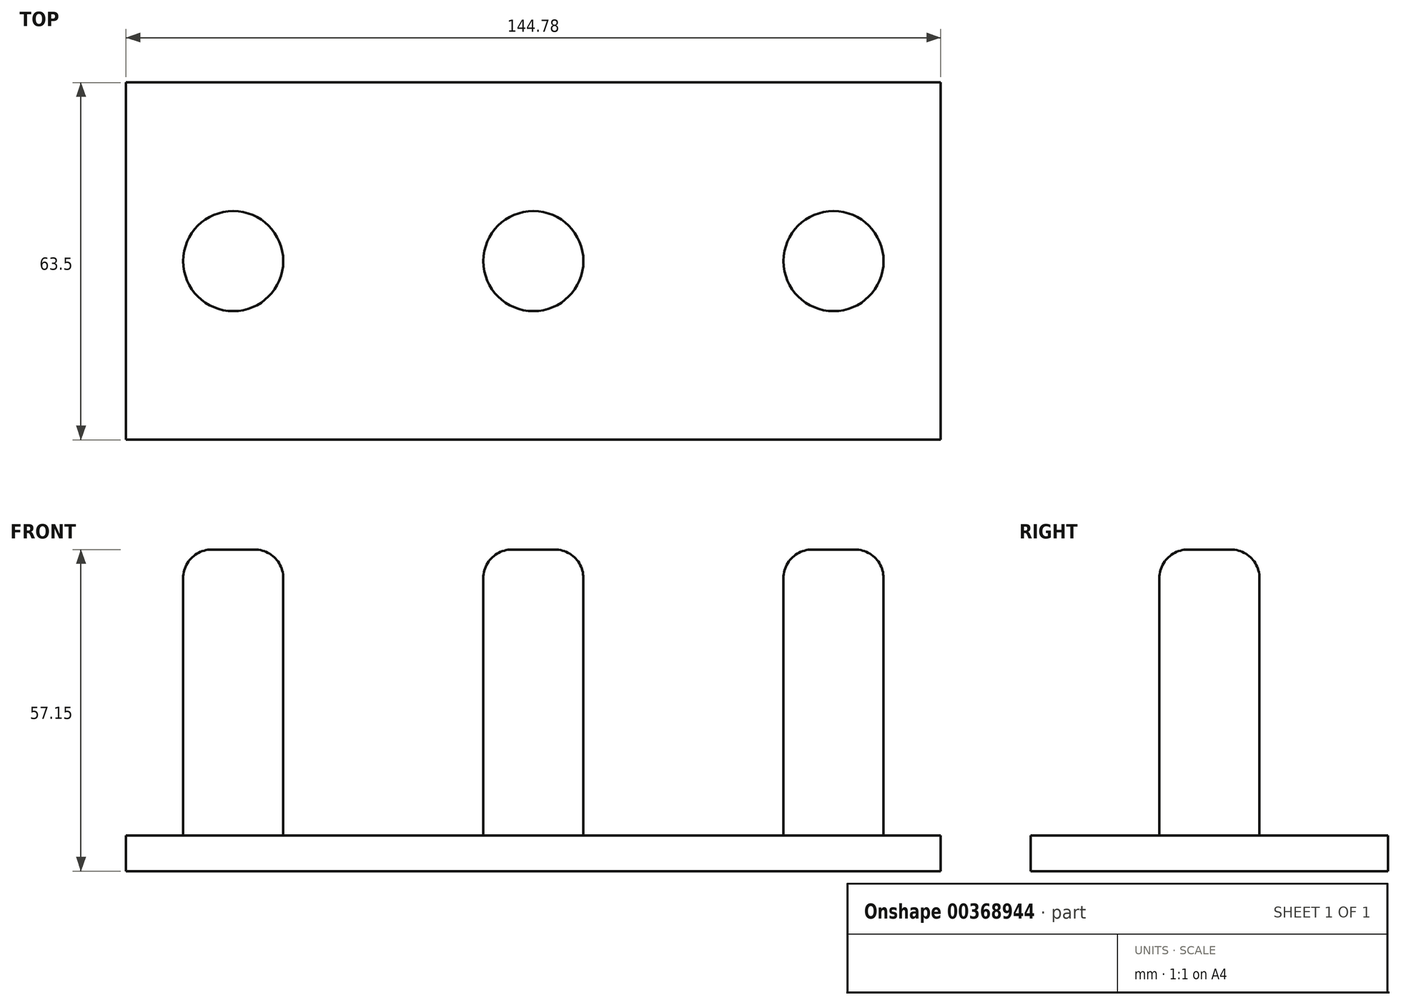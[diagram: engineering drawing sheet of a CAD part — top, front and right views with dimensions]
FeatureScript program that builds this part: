
annotation { "Feature Type Name" : "Feature", "Feature Type Description" : "" }
export const myFeature = defineFeature(function(context is Context, id is Id, definition is map)
    precondition{}
    {
        {
            var Q0;
            Q0=qCreatedBy(makeId("Top.planeOp"),FACE);
            var sketch = newSketch(context, id + "F0", { "sketchPlane" : qUnion([Q0])});
            skLineSegment(sketch, "E0.bottom", {"start": v(-56.5, 25.18) * mm, "end": v(88.28, 25.18) * mm});
            skLineSegment(sketch, "E0.top", {"start": v(-56.5, -38.32) * mm, "end": v(88.28, -38.32) * mm});
            skLineSegment(sketch, "E0.left", {"start": v(-56.5, 25.18) * mm, "end": v(-56.5, -38.32) * mm});
            skLineSegment(sketch, "E0.right", {"start": v(88.28, 25.18) * mm, "end": v(88.28, -38.32) * mm});
            skSolve(sketch);
        }
        {
            var Q0;
            Q0=makeQuery(id+"F0.imprint","IMPRINT",FACE,{"disambiguationData":[TD([[makeQuery(id+"F0.imprint","IMPRINT",EDGE,{"derivedFrom":sQuery(id+"F0.wireOp",EDGE,"E0.bottom")}),-1.0]])]});
            extrude(context, id + "F1", {"entities" : qUnion([Q0]), "depth" : 6.35 * mm});
        }
        {
            var Q0;
            Q0=makeQuery(id+"F1.opExtrude","CAP_FACE",FACE,{"disambiguationData":[OSD([sQuery(id+"F0.wireOp",EDGE,"E0.bottom"),sQuery(id+"F0.wireOp",EDGE,"E0.top"),sQuery(id+"F0.wireOp",EDGE,"E0.left"),sQuery(id+"F0.wireOp",EDGE,"E0.right")])],"isStart":false});
            var sketch = newSketch(context, id + "F2", { "sketchPlane" : qUnion([Q0])});
            skCircle(sketch, "E1", {"center": v(-37.45, -6.57) * mm, "radius": 8.9 * mm});
            skCircle(sketch, "E2", {"center": v(15.9, -6.57) * mm, "radius": 8.9 * mm});
            skCircle(sketch, "E3", {"center": v(69.23, -6.57) * mm, "radius": 8.9 * mm});
            skSolve(sketch);
        }
        {
            var Q0;
            Q0=makeQuery(id+"F2.imprint","IMPRINT",FACE,{"disambiguationData":[TD([[makeQuery(id+"F2.imprint","IMPRINT",EDGE,{"derivedFrom":sQuery(id+"F2.wireOp",EDGE,"E1")}),1.0]])]});
            var Q1;
            Q1=makeQuery(id+"F2.imprint","IMPRINT",FACE,{"disambiguationData":[TD([[makeQuery(id+"F2.imprint","IMPRINT",EDGE,{"derivedFrom":sQuery(id+"F2.wireOp",EDGE,"E2")}),1.0]])]});
            var Q2;
            Q2=makeQuery(id+"F2.imprint","IMPRINT",FACE,{"disambiguationData":[TD([[makeQuery(id+"F2.imprint","IMPRINT",EDGE,{"derivedFrom":sQuery(id+"F2.wireOp",EDGE,"E3")}),1.0]])]});
            extrude(context, id + "F3", {"entities" : qUnion([Q0, Q1, Q2]), "operationType" : NewBodyOperationType.ADD, "depth" : 50.8 * mm});
        }
        {
            var Q0;
            Q0=makeQuery(id+"F3.opExtrude","CAP_EDGE",EDGE,{"disambiguationData":[OSD([sQuery(id+"F2.wireOp",EDGE,"E3")])],"isStart":false});
            var Q1;
            Q1=makeQuery(id+"F3.opExtrude","CAP_EDGE",EDGE,{"disambiguationData":[OSD([sQuery(id+"F2.wireOp",EDGE,"E2")])],"isStart":false});
            var Q2;
            Q2=makeQuery(id+"F3.opExtrude","CAP_EDGE",EDGE,{"disambiguationData":[OSD([sQuery(id+"F2.wireOp",EDGE,"E1")])],"isStart":false});
            fillet(context, id + "F4", {"entities" : qUnion([Q0, Q1, Q2]), "radius" : 5.08 * mm, "tangentPropagation" : true, "allowEdgeOverflow" : false});
        }
    });
